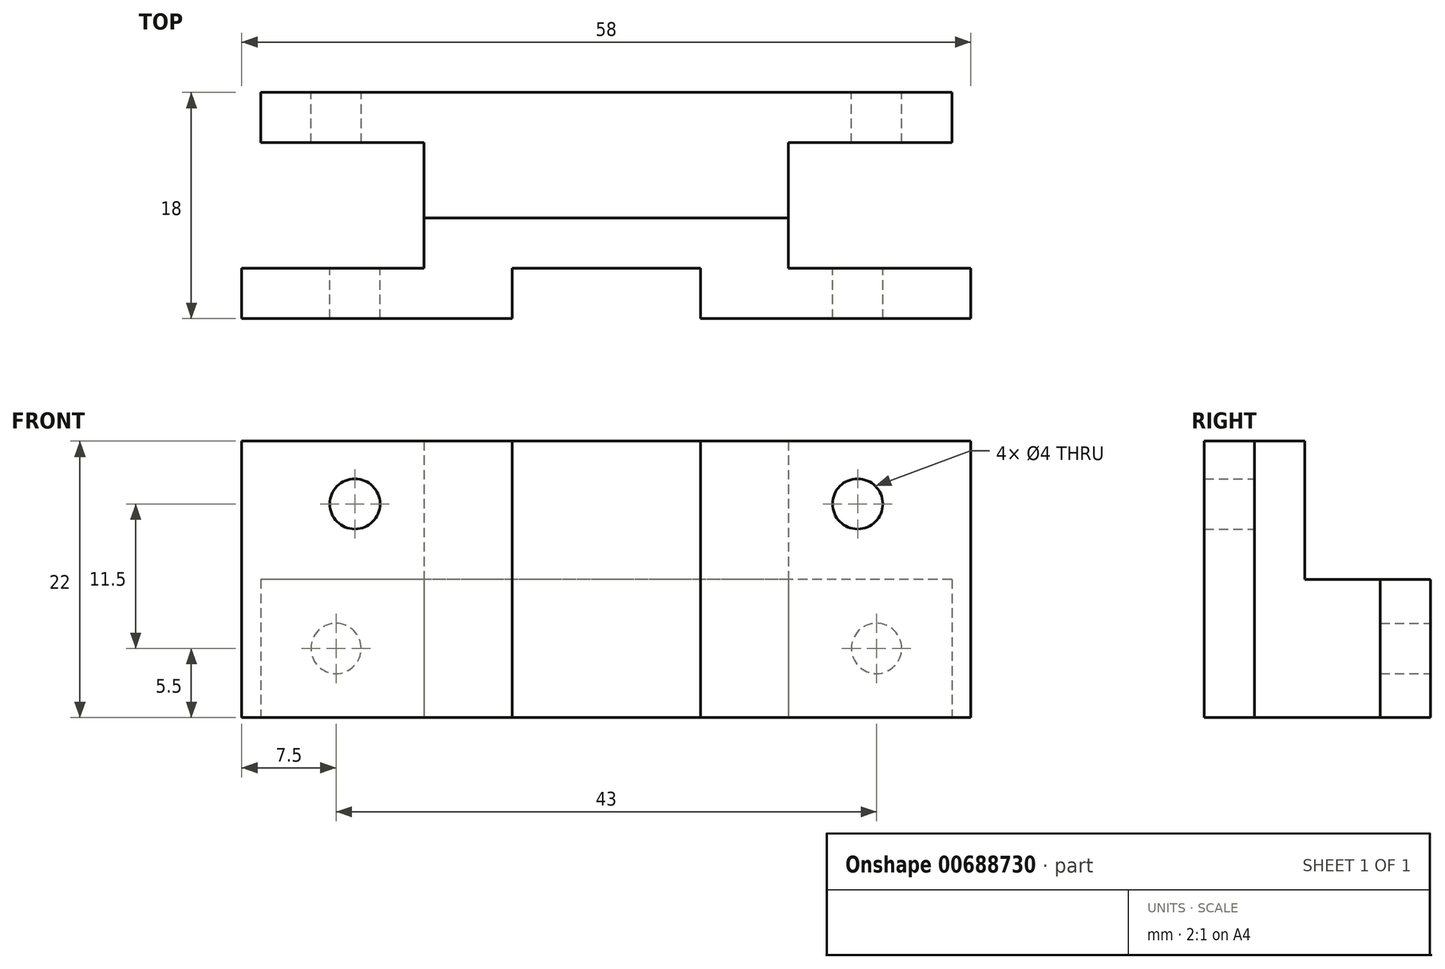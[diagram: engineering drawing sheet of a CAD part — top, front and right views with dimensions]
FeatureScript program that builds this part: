
annotation { "Feature Type Name" : "Feature", "Feature Type Description" : "" }
export const myFeature = defineFeature(function(context is Context, id is Id, definition is map)
    precondition{}
    {
        {
            var Q0;
            Q0=qCreatedBy(makeId("Front.planeOp"),FACE);
            var sketch = newSketch(context, id + "F0", { "sketchPlane" : qUnion([Q0])});
            skLineSegment(sketch, "E0.bottom", {"start": v(-29, 5) * mm, "end": v(29, 5) * mm});
            skLineSegment(sketch, "E0.top", {"start": v(-29, -5) * mm, "end": v(29, -5) * mm});
            skLineSegment(sketch, "E0.left", {"start": v(-29, 5) * mm, "end": v(-29, -5) * mm});
            skLineSegment(sketch, "E0.right", {"start": v(29, 5) * mm, "end": v(29, -5) * mm});
            skPoint(sketch, "E0.middle", {"position": v(0, 0) * mm});
            skLineSegment(sketch, "E1", {"start": v(0, 0) * mm, "end": v(-20, 0) * mm});
            skLineSegment(sketch, "E2", {"start": v(0, 0) * mm, "end": v(20, 0) * mm});
            skCircle(sketch, "E3", {"center": v(-20, 0) * mm, "radius": 2 * mm});
            skCircle(sketch, "E4", {"center": v(20, 0) * mm, "radius": 2 * mm});
            skSolve(sketch);
        }
        {
            var Q0;
            Q0=makeQuery(id+"F0.imprint","IMPRINT",FACE,{"disambiguationData":[TD([[makeQuery(id+"F0.imprint","IMPRINT",EDGE,{"derivedFrom":sQuery(id+"F0.wireOp",EDGE,"E0.bottom")}),-1.0]])]});
            extrude(context, id + "F1", {"entities" : qUnion([Q0]), "depth" : 4 * mm, "offsetDistance" : 25 * mm});
        }
        {
            var Q0;
            Q0=makeQuery(id+"F1.opExtrude","CAP_FACE",FACE,{"disambiguationData":[OSD([sQuery(id+"F0.wireOp",EDGE,"E0.bottom"),sQuery(id+"F0.wireOp",EDGE,"E0.top"),sQuery(id+"F0.wireOp",EDGE,"E0.left"),sQuery(id+"F0.wireOp",EDGE,"E0.right"),sQuery(id+"F0.wireOp",EDGE,"E3"),sQuery(id+"F0.wireOp",EDGE,"E4")])],"isStart":true});
            var sketch = newSketch(context, id + "F2", { "sketchPlane" : qUnion([Q0])});
            skLineSegment(sketch, "E5.bottom", {"start": v(-14.5, 5) * mm, "end": v(14.5, 5) * mm});
            skLineSegment(sketch, "E5.top", {"start": v(-14.5, -5) * mm, "end": v(14.5, -5) * mm});
            skLineSegment(sketch, "E5.left", {"start": v(-14.5, 5) * mm, "end": v(-14.5, -5) * mm});
            skLineSegment(sketch, "E5.right", {"start": v(14.5, 5) * mm, "end": v(14.5, -5) * mm});
            skPoint(sketch, "E5.middle", {"position": v(0, 0) * mm});
            skSolve(sketch);
        }
        {
            var Q0;
            Q0=makeQuery(id+"F2.imprint","IMPRINT",FACE,{"disambiguationData":[TD([[makeQuery(id+"F2.imprint","IMPRINT",EDGE,{"derivedFrom":sQuery(id+"F2.wireOp",EDGE,"E5.bottom")}),1.0]])]});
            extrude(context, id + "F3", {"entities" : qUnion([Q0]), "operationType" : NewBodyOperationType.ADD, "depth" : 4 * mm, "offsetDistance" : 25 * mm});
        }
        {
            var Q0;
            Q0=makeQuery(id+"F1.opExtrude","CAP_FACE",FACE,{"disambiguationData":[OSD([sQuery(id+"F0.wireOp",EDGE,"E0.bottom"),sQuery(id+"F0.wireOp",EDGE,"E0.top"),sQuery(id+"F0.wireOp",EDGE,"E0.left"),sQuery(id+"F0.wireOp",EDGE,"E0.right"),sQuery(id+"F0.wireOp",EDGE,"E3"),sQuery(id+"F0.wireOp",EDGE,"E4")])],"isStart":false});
            var sketch = newSketch(context, id + "F4", { "sketchPlane" : qUnion([Q0])});
            skLineSegment(sketch, "E6.bottom", {"start": v(-7.5, 5) * mm, "end": v(7.5, 5) * mm});
            skLineSegment(sketch, "E6.top", {"start": v(-7.5, -5) * mm, "end": v(7.5, -5) * mm});
            skLineSegment(sketch, "E6.left", {"start": v(-7.5, 5) * mm, "end": v(-7.5, -5) * mm});
            skLineSegment(sketch, "E6.right", {"start": v(7.5, 5) * mm, "end": v(7.5, -5) * mm});
            skPoint(sketch, "E6.middle", {"position": v(0, 0) * mm});
            skSolve(sketch);
        }
        {
            var Q0;
            Q0=qSketchRegion(id+"F4",true);
            extrude(context, id + "F5", {"entities" : qUnion([Q0]), "operationType" : NewBodyOperationType.REMOVE, "oppositeDirection" : true, "depth" : 4 * mm, "offsetDistance" : 25 * mm});
        }
        {
            var Q0;
            Q0=makeQuery(id+"F3.boolean.opBoolean","MERGE",FACE,{"derivedFrom":[makeQuery(id+"F1.opExtrude","SWEPT_FACE",FACE,{"disambiguationData":[OSD([sQuery(id+"F0.wireOp",EDGE,"E0.top")])]}),makeQuery(id+"F3.opExtrude","SWEPT_FACE",FACE,{"disambiguationData":[OSD([sQuery(id+"F2.wireOp",EDGE,"E5.top")])]})]});
            extrude(context, id + "F6", {"entities" : qUnion([Q0]), "operationType" : NewBodyOperationType.ADD, "depth" : 12 * mm, "offsetDistance" : 25 * mm});
        }
        {
            var Q0;
            {var subQ0=sQuery(id+"F2.wireOp",EDGE,"E5.top");Q0=makeQuery(id+"F6.boolean.opBoolean","MERGE",FACE,{"derivedFrom":[makeQuery(id+"F3.opExtrude","CAP_FACE",FACE,{"disambiguationData":[OSD([sQuery(id+"F2.wireOp",EDGE,"E5.bottom"),subQ0,sQuery(id+"F2.wireOp",EDGE,"E5.left"),sQuery(id+"F2.wireOp",EDGE,"E5.right")])],"isStart":false}),makeQuery(id+"F6.opExtrude","SWEPT_FACE",FACE,{"disambiguationData":[OSD([subQ0])]})]});}
            var sketch = newSketch(context, id + "F7", { "sketchPlane" : qUnion([Q0])});
            skLineSegment(sketch, "E7.bottom", {"start": v(-14.5, -17) * mm, "end": v(14.5, -17) * mm});
            skLineSegment(sketch, "E7.top", {"start": v(-14.5, -6) * mm, "end": v(14.5, -6) * mm});
            skLineSegment(sketch, "E7.left", {"start": v(-14.5, -17) * mm, "end": v(-14.5, -6) * mm});
            skLineSegment(sketch, "E7.right", {"start": v(14.5, -17) * mm, "end": v(14.5, -6) * mm});
            skSolve(sketch);
        }
        {
            var Q0;
            Q0=qSketchRegion(id+"F7",true);
            extrude(context, id + "F8", {"entities" : qUnion([Q0]), "operationType" : NewBodyOperationType.ADD, "depth" : 6 * mm, "offsetDistance" : 25 * mm});
        }
        {
            var Q0;
            Q0=makeQuery(id+"F8.opExtrude","CAP_FACE",FACE,{"disambiguationData":[OSD([sQuery(id+"F7.wireOp",EDGE,"E7.bottom"),sQuery(id+"F7.wireOp",EDGE,"E7.top"),sQuery(id+"F7.wireOp",EDGE,"E7.left"),sQuery(id+"F7.wireOp",EDGE,"E7.right")])],"isStart":false});
            var sketch = newSketch(context, id + "F9", { "sketchPlane" : qUnion([Q0])});
            skLineSegment(sketch, "E8.bottom", {"start": v(-27.5, -6) * mm, "end": v(27.5, -6) * mm});
            skLineSegment(sketch, "E8.top", {"start": v(-27.5, -17) * mm, "end": v(27.5, -17) * mm});
            skLineSegment(sketch, "E8.left", {"start": v(-27.5, -6) * mm, "end": v(-27.5, -17) * mm});
            skLineSegment(sketch, "E8.right", {"start": v(27.5, -6) * mm, "end": v(27.5, -17) * mm});
            skPoint(sketch, "E8.middle", {"position": v(0, -11.5) * mm});
            skPoint(sketch, "E8.middle.positionSnap0", {"position": v(-14.5, -11.5) * mm});
            skPoint(sketch, "E8.middle.positionSnap1", {"position": v(0, -6) * mm});
            skPoint(sketch, "E8.cornerSnap0", {"position": v(0, -6) * mm});
            skPoint(sketch, "E8.centerSnap0", {"position": v(-14.5, -11.5) * mm});
            skPoint(sketch, "E8.centerSnap1", {"position": v(0, -6) * mm});
            skSolve(sketch);
        }
        {
            var Q0;
            {var subQ1=makeQuery(id+"F8.opExtrude","CAP_EDGE",EDGE,{"disambiguationData":[OSD([sQuery(id+"F7.wireOp",EDGE,"E7.left")])],"isStart":false});Q0=makeQuery(id+"F9.imprint","IMPRINT",FACE,{"disambiguationData":[TD([[makeQuery(id+"F9.imprint","IMPRINT",EDGE,{"derivedFrom":subQ1}),1.0]])]});}
            var Q1;
            {var subQ2=sQuery(id+"F9.wireOp",EDGE,"E8.left");Q1=makeQuery(id+"F9.imprint","IMPRINT",FACE,{"disambiguationData":[TD([[makeQuery(id+"F9.imprint","IMPRINT",EDGE,{"derivedFrom":subQ2}),1.0]])]});}
            var Q2;
            {var subQ2=sQuery(id+"F9.wireOp",EDGE,"E8.right");Q2=makeQuery(id+"F9.imprint","IMPRINT",FACE,{"disambiguationData":[TD([[makeQuery(id+"F9.imprint","IMPRINT",EDGE,{"derivedFrom":subQ2}),-1.0]])]});}
            extrude(context, id + "F10", {"entities" : qUnion([Q0, Q1, Q2]), "operationType" : NewBodyOperationType.ADD, "depth" : 4 * mm, "offsetDistance" : 25 * mm});
        }
        {
            var Q0;
            Q0=makeQuery(id+"F10.opExtrude","CAP_FACE",FACE,{"disambiguationData":[OSD([sQuery(id+"F9.wireOp",EDGE,"E8.bottom"),sQuery(id+"F9.wireOp",EDGE,"E8.top"),sQuery(id+"F9.wireOp",EDGE,"E8.left"),sQuery(id+"F9.wireOp",EDGE,"E8.right")])],"isStart":false});
            var sketch = newSketch(context, id + "F11", { "sketchPlane" : qUnion([Q0])});
            skLineSegment(sketch, "E9", {"start": v(0, -11.5) * mm, "end": v(-21.5, -11.5) * mm});
            skPoint(sketch, "E9.startSnap0", {"position": v(-27.5, -11.5) * mm});
            skPoint(sketch, "E9.startSnap1", {"position": v(0, -6) * mm});
            skLineSegment(sketch, "E10", {"start": v(0, -11.5) * mm, "end": v(21.5, -11.5) * mm});
            skCircle(sketch, "E11", {"center": v(-21.5, -11.5) * mm, "radius": 2 * mm});
            skCircle(sketch, "E12", {"center": v(21.5, -11.5) * mm, "radius": 2 * mm});
            skSolve(sketch);
        }
        {
            var Q0;
            Q0=makeQuery(id+"F11.imprint","IMPRINT",FACE,{"disambiguationData":[TD([[makeQuery(id+"F11.imprint","IMPRINT",EDGE,{"derivedFrom":sQuery(id+"F11.wireOp",EDGE,"E11")}),1.0]])]});
            var Q1;
            Q1=makeQuery(id+"F11.imprint","IMPRINT",FACE,{"disambiguationData":[TD([[makeQuery(id+"F11.imprint","IMPRINT",EDGE,{"derivedFrom":sQuery(id+"F11.wireOp",EDGE,"E12")}),1.0]])]});
            extrude(context, id + "F12", {"entities" : qUnion([Q0, Q1]), "operationType" : NewBodyOperationType.REMOVE, "oppositeDirection" : true, "depth" : 4 * mm, "offsetDistance" : 25 * mm});
        }
    });
